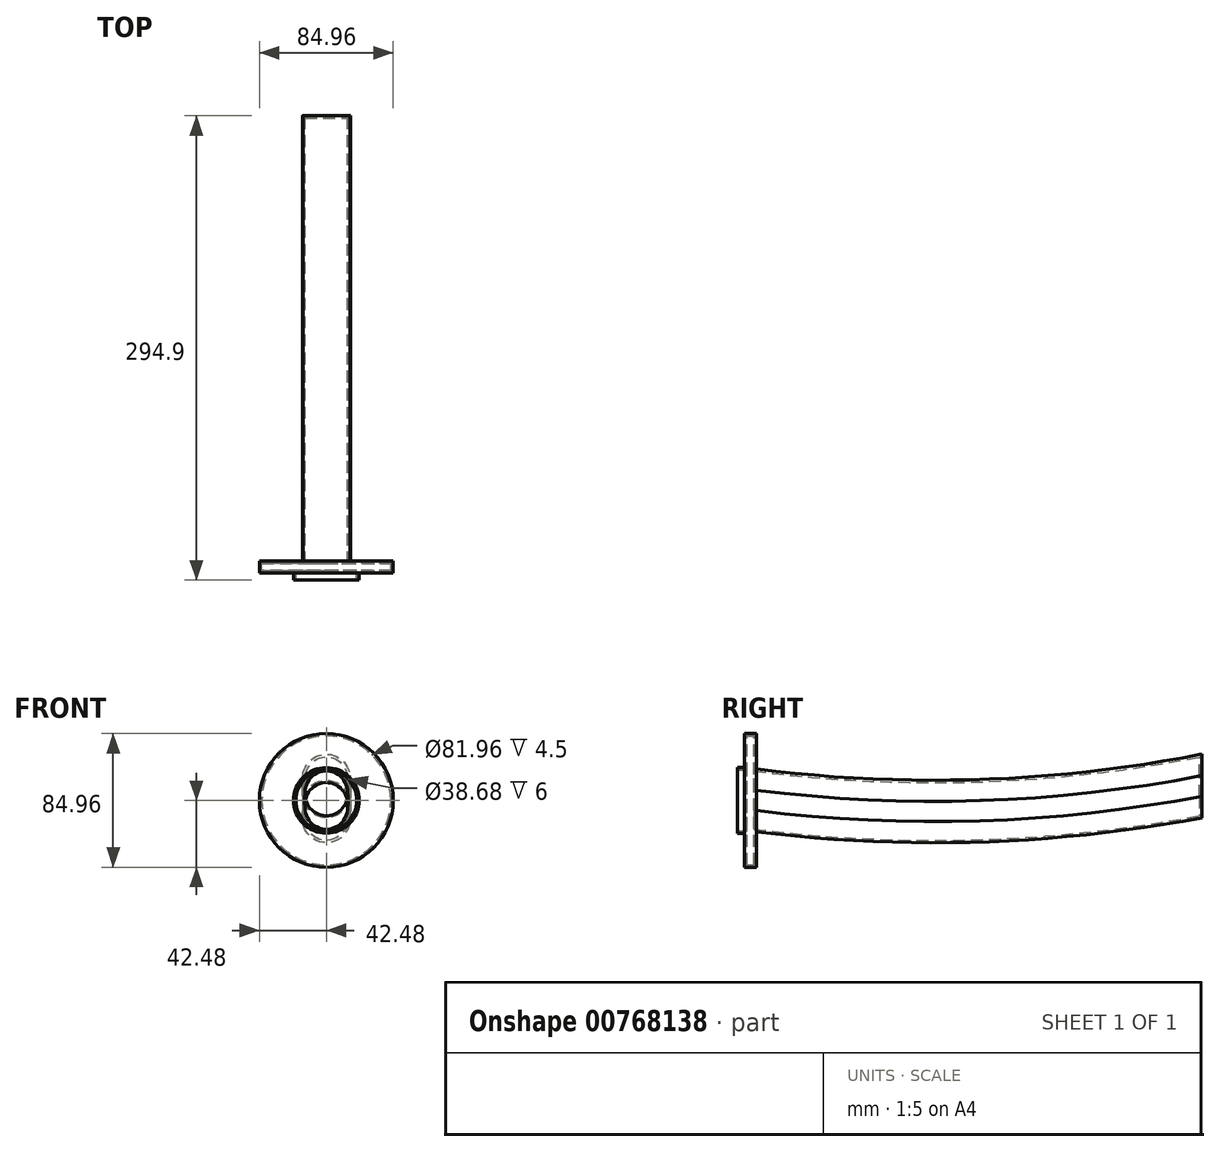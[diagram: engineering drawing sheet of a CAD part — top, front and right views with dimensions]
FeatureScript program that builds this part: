
annotation { "Feature Type Name" : "Feature", "Feature Type Description" : "" }
export const myFeature = defineFeature(function(context is Context, id is Id, definition is map)
    precondition{}
    {
        {
            var Q0;
            Q0=qCreatedBy(makeId("Front.planeOp"),FACE);
            var sketch = newSketch(context, id + "F0", { "sketchPlane" : qUnion([Q0])});
            skLineSegment(sketch, "E0", {"start": v(0, 20) * mm, "end": v(0, -20) * mm, "construction": true});
            skLineSegment(sketch, "E1", {"start": v(0, 0) * mm, "end": v(-22.88, 0) * mm, "construction": true});
            skArc(sketch, "E2", {"start": v(-14.93, 6.47) * mm, "mid": v(-15.25, 0) * mm, "end": v(-14.93, -6.47) * mm});
            skArc(sketch, "E3.trimOffspring", {"start": v(0, 20) * mm, "mid": v(-10.07, 16.12) * mm, "end": v(-14.93, 6.47) * mm});
            skArc(sketch, "E4.trimOffspring", {"start": v(0, -20) * mm, "mid": v(-10.07, -16.12) * mm, "end": v(-14.93, -6.47) * mm});
            skArc(sketch, "E5.MirrorCS", {"start": v(0, 20) * mm, "mid": v(10.07, 16.12) * mm, "end": v(14.93, 6.47) * mm});
            skArc(sketch, "E6.MirrorCS", {"start": v(14.93, 6.47) * mm, "mid": v(15.25, 0) * mm, "end": v(14.93, -6.47) * mm});
            skArc(sketch, "E7.MirrorCS", {"start": v(0, -20) * mm, "mid": v(10.07, -16.12) * mm, "end": v(14.93, -6.47) * mm});
            skSolve(sketch);
        }
        {
            var Q0;
            Q0=qCreatedBy(makeId("Right.planeOp"),FACE);
            var sketch = newSketch(context, id + "F1", { "sketchPlane" : qUnion([Q0])});
            skArc(sketch, "E8", {"start": v(0, 0.3) * mm, "mid": v(145.07, -6.15) * mm, "end": v(289.3, 10.73) * mm});
            skSolve(sketch);
        }
        {
            var Q0;
            Q0=makeQuery(id+"F0.imprint","IMPRINT",FACE,{"disambiguationData":[TD([[makeQuery(id+"F0.imprint","IMPRINT",EDGE,{"derivedFrom":sQuery(id+"F0.wireOp",EDGE,"E2")}),1.0]])]});
            var Q1;
            Q1=sQuery(id+"F1.wireOp",EDGE,"E8");
            sweep(context, id + "F2", {"profiles" : qUnion([Q0]), "path" : qUnion([Q1])});
        }
        {
            var Q0;
            Q0=qCreatedBy(makeId("Front.planeOp"),FACE);
            cPlane(context, id + "F3", {"entities" : qUnion([Q0]), "cplaneType" : CPlaneType.OFFSET, "offset" : 298 * mm, "oppositeDirection" : true, "width" : 150 * mm, "height" : 150 * mm});
        }
        {
            var Q0;
            Q0=qCreatedBy(id+"F3.planeOp",FACE);
            var sketch = newSketch(context, id + "F4", { "sketchPlane" : qUnion([Q0])});
            skLineSegment(sketch, "E9.bottom", {"start": v(26.55, 36.19) * mm, "end": v(-26.55, 36.19) * mm});
            skLineSegment(sketch, "E9.top", {"start": v(26.55, -36.19) * mm, "end": v(-26.55, -36.19) * mm});
            skLineSegment(sketch, "E9.left", {"start": v(26.55, 36.19) * mm, "end": v(26.55, -36.19) * mm});
            skLineSegment(sketch, "E9.right", {"start": v(-26.55, 36.19) * mm, "end": v(-26.55, -36.19) * mm});
            skPoint(sketch, "E9.middle", {"position": v(0, 0) * mm});
            skSolve(sketch);
        }
        {
            var Q0;
            Q0=makeQuery(id+"F4.imprint","IMPRINT",FACE,{"disambiguationData":[TD([[makeQuery(id+"F4.imprint","IMPRINT",EDGE,{"derivedFrom":sQuery(id+"F4.wireOp",EDGE,"E9.bottom")}),1.0]])]});
            extrude(context, id + "F5", {"entities" : qUnion([Q0]), "operationType" : NewBodyOperationType.REMOVE, "depth" : 15.1 * mm, "offsetDistance" : 25 * mm});
        }
        {
            var Q0;
            Q0=qCreatedBy(makeId("Front.planeOp"),FACE);
            var sketch = newSketch(context, id + "F6", { "sketchPlane" : qUnion([Q0])});
            skCircle(sketch, "E10", {"center": v(0, 0) * mm, "radius": 42.48 * mm});
            skSolve(sketch);
        }
        {
            var Q0;
            Q0=makeQuery(id+"F6.imprint","IMPRINT",FACE,{"disambiguationData":[TD([[makeQuery(id+"F6.imprint","IMPRINT",EDGE,{"derivedFrom":sQuery(id+"F6.wireOp",EDGE,"E10")}),1.0]])]});
            extrude(context, id + "F7", {"entities" : qUnion([Q0]), "operationType" : NewBodyOperationType.ADD, "depth" : 7.5 * mm, "offsetDistance" : 25 * mm});
        }
        {
            var Q0;
            Q0=makeQuery(id+"F7.opExtrude","CAP_FACE",FACE,{"disambiguationData":[OSD([sQuery(id+"F6.wireOp",EDGE,"E10")])],"isStart":false});
            var sketch = newSketch(context, id + "F8", { "sketchPlane" : qUnion([Q0])});
            skCircle(sketch, "E11", {"center": v(0, 0) * mm, "radius": 20.84 * mm});
            skSolve(sketch);
        }
        {
            var Q0;
            Q0 = qSketchRegion(id + "F8", true);
            extrude(context, id + "F9", {"entities" : qUnion([Q0]), "operationType" : NewBodyOperationType.ADD, "depth" : 4.5 * mm, "offsetDistance" : 25 * mm});
        }
        {
            var Q0;
            Q0=makeQuery(id+"F9.opExtrude","CAP_FACE",FACE,{"disambiguationData":[OSD([sQuery(id+"F8.wireOp",EDGE,"E11")])],"isStart":false});
            shell(context, id + "F10", {"entities" : qUnion([Q0]), "thickness" : 1.5 * mm});
        }
    });
